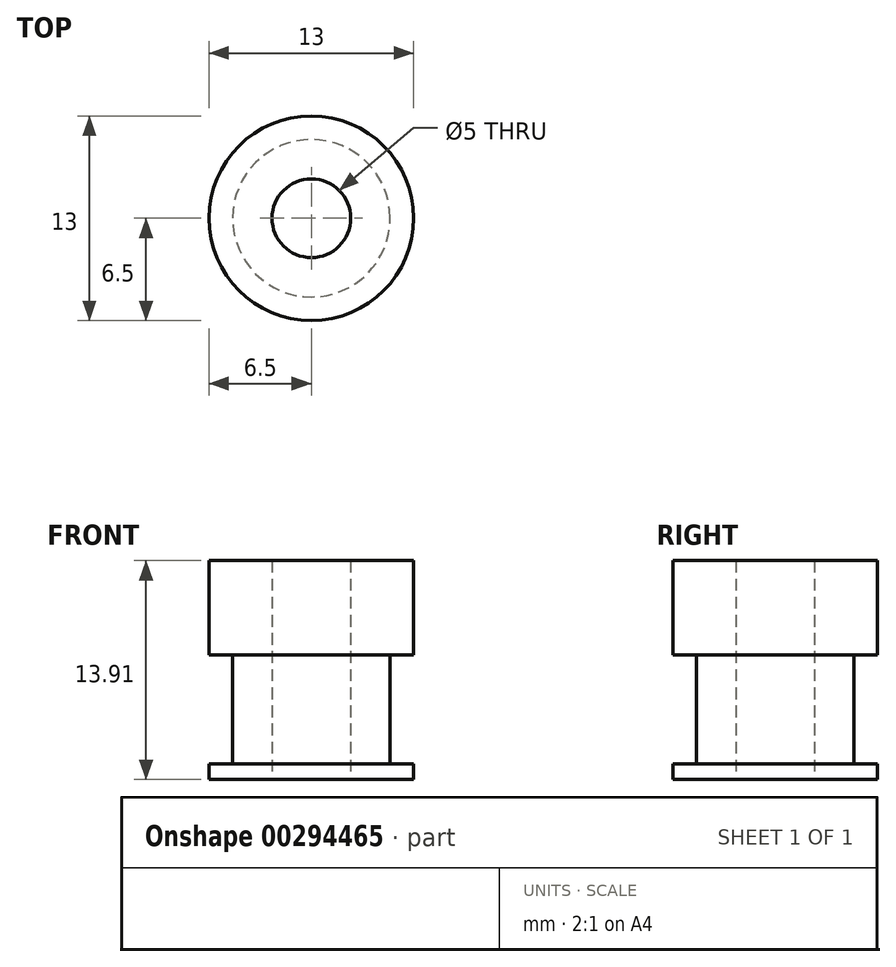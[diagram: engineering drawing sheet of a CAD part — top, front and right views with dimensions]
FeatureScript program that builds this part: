
annotation { "Feature Type Name" : "Feature", "Feature Type Description" : "" }
export const myFeature = defineFeature(function(context is Context, id is Id, definition is map)
    precondition{}
    {
        {
            var Q0;
            Q0=qCreatedBy(makeId("Front.planeOp"),FACE);
            var sketch = newSketch(context, id + "F0", { "sketchPlane" : qUnion([Q0])});
            skLineSegment(sketch, "E0", {"start": v(0, 0) * mm, "end": v(0, 13.9) * mm, "construction": true});
            skLineSegment(sketch, "E1", {"start": v(2.5, 0) * mm, "end": v(6.5, 0) * mm});
            skLineSegment(sketch, "E2", {"start": v(6.5, 0) * mm, "end": v(6.5, 1) * mm});
            skLineSegment(sketch, "E3", {"start": v(6.5, 1) * mm, "end": v(5, 1) * mm});
            skLineSegment(sketch, "E4", {"start": v(5, 1) * mm, "end": v(5, 7.9) * mm});
            skLineSegment(sketch, "E5", {"start": v(6.5, 7.9) * mm, "end": v(6.5, 13.9) * mm});
            skLineSegment(sketch, "E6", {"start": v(6.5, 13.9) * mm, "end": v(2.5, 13.9) * mm});
            skLineSegment(sketch, "E7", {"start": v(2.5, 13.9) * mm, "end": v(2.5, 0) * mm});
            skLineSegment(sketch, "E8", {"start": v(5, 7.9) * mm, "end": v(6.5, 7.9) * mm});
            skSolve(sketch);
        }
        {
            var Q0;
            Q0 = qSketchRegion(id + "F0", true);
            var Q1;
            Q1=sQuery(id+"F0.wireOp",EDGE,"E0");
            revolve(context, id + "F1", {"entities" : qUnion([Q0]), "axis" : qUnion([Q1]), "revolveType" : RevolveType.FULL});
        }
    });
